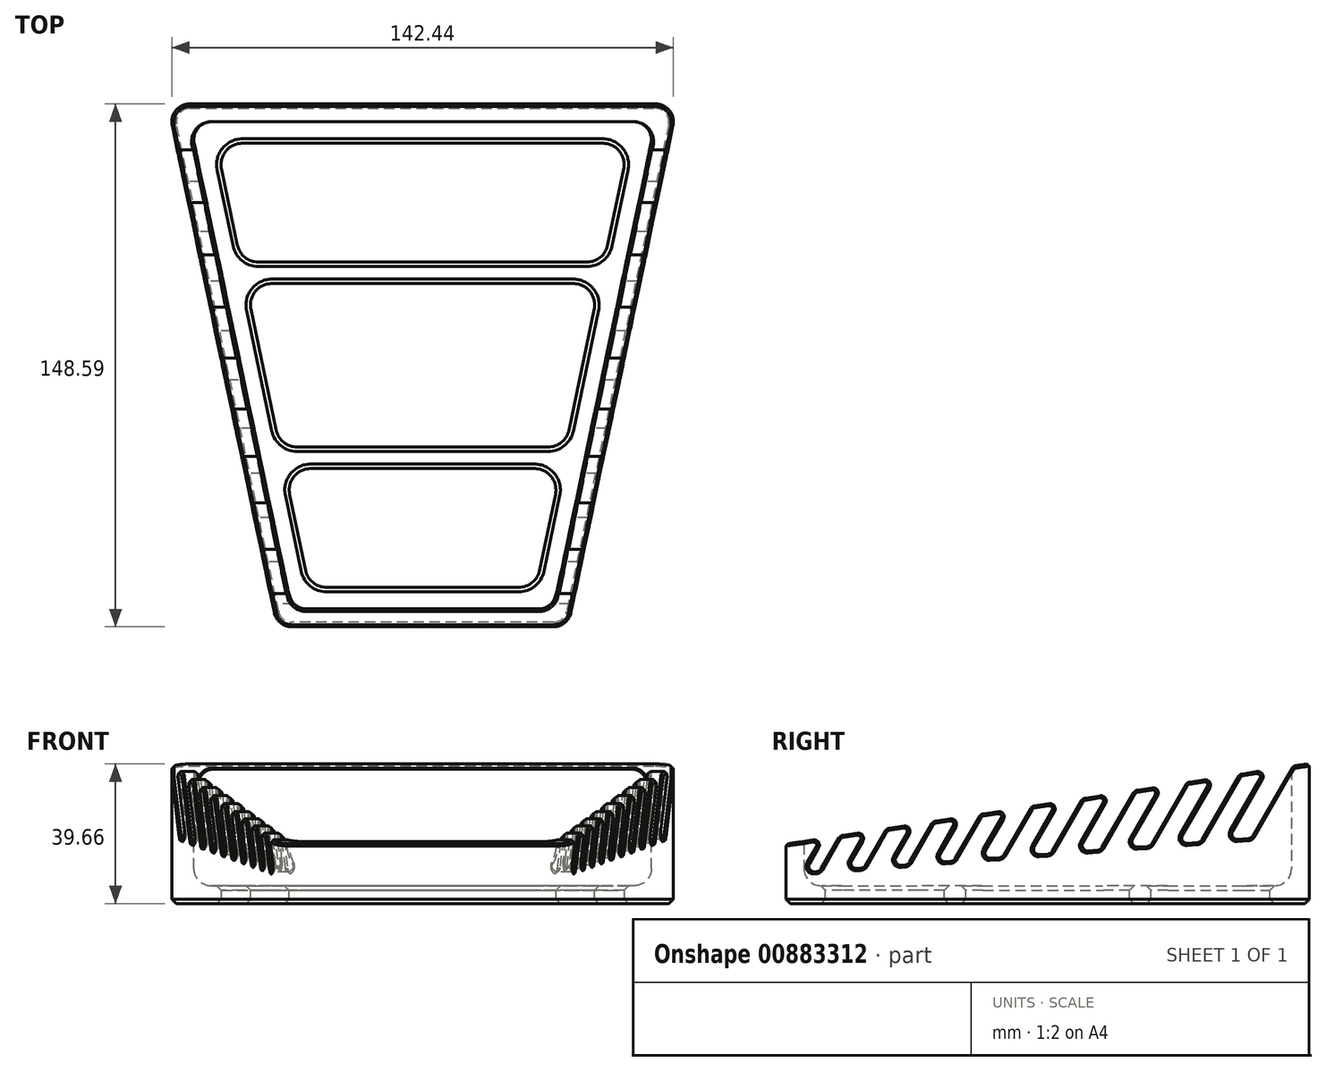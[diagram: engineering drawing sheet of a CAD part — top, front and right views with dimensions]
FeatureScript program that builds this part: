
annotation { "Feature Type Name" : "Feature", "Feature Type Description" : "" }
export const myFeature = defineFeature(function(context is Context, id is Id, definition is map)
    precondition{}
    {
        {
            var Q0;
            Q0=qCreatedBy(makeId("Top.planeOp"),FACE);
            var sketch = newSketch(context, id + "F0", { "sketchPlane" : qUnion([Q0])});
            skLineSegment(sketch, "E0", {"start": v(0, 200.12) * mm, "end": v(0, 0) * mm, "construction": true});
            skLineSegment(sketch, "E1", {"start": v(0, 0) * mm, "end": v(243.38, 0) * mm, "construction": true});
            skLineSegment(sketch, "E2", {"start": v(-72.4, 148.6) * mm, "end": v(72.4, 148.6) * mm});
            skLineSegment(sketch, "E3", {"start": v(72.4, 148.6) * mm, "end": v(41.28, 0) * mm});
            skLineSegment(sketch, "E4", {"start": v(41.28, 0) * mm, "end": v(-41.27, 0) * mm});
            skLineSegment(sketch, "E5", {"start": v(-41.27, 0) * mm, "end": v(-72.4, 148.6) * mm});
            skSolve(sketch);
        }
        {
            var Q0;
            Q0=makeQuery(id+"F0.imprint","IMPRINT",FACE,{"disambiguationData":[TD([[makeQuery(id+"F0.imprint","IMPRINT",EDGE,{"derivedFrom":sQuery(id+"F0.wireOp",EDGE,"E2")}),-1.0]])]});
            extrude(context, id + "F1", {"entities" : qUnion([Q0]), "depth" : 50.8 * mm, "offsetDistance" : 25.4 * mm});
        }
        {
            var Q0;
            Q0=qCreatedBy(makeId("Right.planeOp"),FACE);
            var sketch = newSketch(context, id + "F2", { "sketchPlane" : qUnion([Q0])});
            skLineSegment(sketch, "E6", {"start": v(0, 88.7) * mm, "end": v(0, 0) * mm, "construction": true});
            skLineSegment(sketch, "E7", {"start": v(0, 0) * mm, "end": v(187.78, 0) * mm, "construction": true});
            skCircle(sketch, "E8", {"center": v(130.24, 18.35) * mm, "radius": 18.35 * mm, "construction": true});
            skLineSegment(sketch, "E9", {"start": v(130.24, 18.35) * mm, "end": v(9.08, 9.08) * mm, "construction": true});
            skLineSegment(sketch, "E10", {"start": v(17.54, 5.78) * mm, "end": v(114.68, 8.63) * mm, "construction": true});
            skCircle(sketch, "E11", {"center": v(9.08, 9.08) * mm, "radius": 9.08 * mm, "construction": true});
            skLineSegment(sketch, "E12", {"start": v(127.45, 36.49) * mm, "end": v(7.7, 18.06) * mm, "construction": true});
            skSolve(sketch);
        }
        {
            var Q0;
            Q0=makeQuery(id+"F1.opExtrude","CAP_FACE",FACE,{"disambiguationData":[OSD([sQuery(id+"F0.wireOp",EDGE,"E2"),sQuery(id+"F0.wireOp",EDGE,"E3"),sQuery(id+"F0.wireOp",EDGE,"E4"),sQuery(id+"F0.wireOp",EDGE,"E5")])],"isStart":false});
            shell(context, id + "F3", {"entities" : qUnion([Q0]), "thickness" : 5.08 * mm});
        }
        {
            var Q0;
            Q0=qCreatedBy(makeId("Right.planeOp"),FACE);
            var sketch = newSketch(context, id + "F4", { "sketchPlane" : qUnion([Q0])});
            skLineSegment(sketch, "E13", {"start": v(0, 69.39) * mm, "end": v(0, 0) * mm, "construction": true});
            skLineSegment(sketch, "E14", {"start": v(0, 0) * mm, "end": v(193.07, 0) * mm, "construction": true});
            skLineSegment(sketch, "E15", {"start": v(-4.75, 16.16) * mm, "end": v(121.9, 35.66) * mm, "construction": true});
            skLineSegment(sketch, "E16", {"start": v(13.1, 18.91) * mm, "end": v(7.35, 8.97) * mm, "construction": true});
            skLineSegment(sketch, "E17", {"start": v(25.97, 20.9) * mm, "end": v(19.63, 9.91) * mm, "construction": true});
            skLineSegment(sketch, "E18", {"start": v(39.17, 22.93) * mm, "end": v(32.2, 10.88) * mm, "construction": true});
            skLineSegment(sketch, "E19", {"start": v(52.53, 24.98) * mm, "end": v(44.94, 11.85) * mm, "construction": true});
            skLineSegment(sketch, "E20", {"start": v(66.53, 27.14) * mm, "end": v(58.3, 12.87) * mm, "construction": true});
            skLineSegment(sketch, "E21", {"start": v(81.01, 29.37) * mm, "end": v(72.1, 13.93) * mm, "construction": true});
            skLineSegment(sketch, "E22", {"start": v(95.66, 31.62) * mm, "end": v(86.06, 15) * mm, "construction": true});
            skLineSegment(sketch, "E23", {"start": v(110.47, 33.9) * mm, "end": v(100.18, 16.08) * mm, "construction": true});
            skLineSegment(sketch, "E24", {"start": v(113.85, 34.42) * mm, "end": v(121.9, 35.66) * mm});
            skLineSegment(sketch, "E25", {"start": v(161.29, 41.72) * mm, "end": v(161.29, 63.5) * mm});
            skLineSegment(sketch, "E26", {"start": v(161.29, 63.5) * mm, "end": v(-12.7, 63.5) * mm});
            skLineSegment(sketch, "E27", {"start": v(-12.7, 63.5) * mm, "end": v(-12.7, 14.94) * mm});
            skLineSegment(sketch, "E28", {"start": v(-12.7, 14.94) * mm, "end": v(10.84, 18.56) * mm});
            skLineSegment(sketch, "E29", {"start": v(113.85, 34.42) * mm, "end": v(103.4, 16.32) * mm});
            skLineSegment(sketch, "E30", {"start": v(96.96, 15.83) * mm, "end": v(107.09, 33.38) * mm});
            skLineSegment(sketch, "E31", {"start": v(107.09, 33.38) * mm, "end": v(99.04, 32.14) * mm});
            skLineSegment(sketch, "E32", {"start": v(99.04, 32.14) * mm, "end": v(89.28, 15.24) * mm});
            skLineSegment(sketch, "E33", {"start": v(82.84, 14.75) * mm, "end": v(92.28, 31.1) * mm});
            skLineSegment(sketch, "E34", {"start": v(92.28, 31.1) * mm, "end": v(84.23, 29.86) * mm});
            skLineSegment(sketch, "E35", {"start": v(84.23, 29.86) * mm, "end": v(75.17, 14.16) * mm});
            skLineSegment(sketch, "E36", {"start": v(69.03, 13.7) * mm, "end": v(77.8, 28.87) * mm});
            skLineSegment(sketch, "E37", {"start": v(77.8, 28.87) * mm, "end": v(69.75, 27.63) * mm});
            skLineSegment(sketch, "E38", {"start": v(69.75, 27.63) * mm, "end": v(61.36, 13.1) * mm});
            skLineSegment(sketch, "E39", {"start": v(55.22, 12.64) * mm, "end": v(63.3, 26.64) * mm});
            skLineSegment(sketch, "E40", {"start": v(63.3, 26.64) * mm, "end": v(55.26, 25.4) * mm});
            skLineSegment(sketch, "E41", {"start": v(55.26, 25.4) * mm, "end": v(47.55, 12.05) * mm});
            skLineSegment(sketch, "E42", {"start": v(42.34, 11.65) * mm, "end": v(49.79, 24.56) * mm});
            skLineSegment(sketch, "E43", {"start": v(49.79, 24.56) * mm, "end": v(41.74, 23.32) * mm});
            skLineSegment(sketch, "E44", {"start": v(41.74, 23.32) * mm, "end": v(34.66, 11.06) * mm});
            skLineSegment(sketch, "E45", {"start": v(29.76, 10.69) * mm, "end": v(36.6, 22.53) * mm});
            skLineSegment(sketch, "E46", {"start": v(36.6, 22.53) * mm, "end": v(28.54, 21.29) * mm});
            skLineSegment(sketch, "E47", {"start": v(28.54, 21.29) * mm, "end": v(22.08, 10.1) * mm});
            skLineSegment(sketch, "E48", {"start": v(17.17, 9.73) * mm, "end": v(23.4, 20.5) * mm});
            skLineSegment(sketch, "E49", {"start": v(23.4, 20.5) * mm, "end": v(15.35, 19.26) * mm});
            skLineSegment(sketch, "E50", {"start": v(15.35, 19.26) * mm, "end": v(9.5, 9.14) * mm});
            skLineSegment(sketch, "E51", {"start": v(5.2, 8.8) * mm, "end": v(10.84, 18.56) * mm});
            skLineSegment(sketch, "E52", {"start": v(5.2, 8.8) * mm, "end": v(146.22, 19.6) * mm, "construction": true});
            skPoint(sketch, "E53.orphan", {"position": v(97.29, 11.07) * mm});
            skLineSegment(sketch, "E54", {"start": v(103.4, 16.32) * mm, "end": v(96.96, 15.83) * mm});
            skLineSegment(sketch, "E55", {"start": v(89.28, 15.24) * mm, "end": v(82.84, 14.75) * mm});
            skLineSegment(sketch, "E56", {"start": v(69.03, 13.7) * mm, "end": v(75.17, 14.16) * mm});
            skLineSegment(sketch, "E57", {"start": v(61.36, 13.1) * mm, "end": v(55.22, 12.64) * mm});
            skLineSegment(sketch, "E58", {"start": v(47.55, 12.05) * mm, "end": v(42.34, 11.65) * mm});
            skLineSegment(sketch, "E59", {"start": v(34.66, 11.06) * mm, "end": v(29.76, 10.69) * mm});
            skLineSegment(sketch, "E60", {"start": v(22.08, 10.1) * mm, "end": v(17.17, 9.73) * mm});
            skLineSegment(sketch, "E61", {"start": v(9.5, 9.14) * mm, "end": v(5.2, 8.8) * mm});
            skLineSegment(sketch, "E62", {"start": v(125.36, 36.2) * mm, "end": v(114.37, 17.16) * mm, "construction": true});
            skLineSegment(sketch, "E63", {"start": v(140.4, 38.5) * mm, "end": v(128.71, 18.26) * mm, "construction": true});
            skLineSegment(sketch, "E64", {"start": v(121.9, 35.66) * mm, "end": v(111.07, 16.91) * mm});
            skLineSegment(sketch, "E65", {"start": v(111.07, 16.91) * mm, "end": v(117.67, 17.42) * mm});
            skLineSegment(sketch, "E66", {"start": v(117.67, 17.42) * mm, "end": v(128.82, 36.73) * mm});
            skLineSegment(sketch, "E67.trimOffspring", {"start": v(128.82, 36.73) * mm, "end": v(136.86, 37.96) * mm, "construction": true});
            skLineSegment(sketch, "E68.trimOffspring", {"start": v(128.82, 36.73) * mm, "end": v(136.86, 37.96) * mm});
            skLineSegment(sketch, "E69", {"start": v(136.86, 37.96) * mm, "end": v(125.34, 18) * mm});
            skLineSegment(sketch, "E70", {"start": v(125.34, 18) * mm, "end": v(132.09, 18.52) * mm});
            skLineSegment(sketch, "E71", {"start": v(132.09, 18.52) * mm, "end": v(143.95, 39.06) * mm});
            skLineSegment(sketch, "E72.trimOffspring", {"start": v(161.29, 41.72) * mm, "end": v(193.55, 46.7) * mm, "construction": true});
            skLineSegment(sketch, "E73.trimOffspring", {"start": v(143.95, 39.06) * mm, "end": v(161.29, 41.72) * mm});
            skSolve(sketch);
        }
        {
            var Q0;
            Q0=qSketchRegion(id+"F4",true);
            extrude(context, id + "F5", {"entities" : qUnion([Q0]), "operationType" : NewBodyOperationType.REMOVE, "endBound" : BoundingType.THROUGH_ALL, "oppositeDirection" : true, "depth" : 25.4 * mm, "offsetDistance" : 25.4 * mm, "hasSecondDirection" : true, "secondDirectionBound" : SecondDirectionBoundingType.THROUGH_ALL, "secondDirectionOppositeDirection" : false, "secondDirectionDepth" : 25.4 * mm});
        }
        {
            var Q0;
            Q0=makeQuery(id+"F3.opShell","OFFSET_FACE",FACE,{"disambiguationData":[OSD([sQuery(id+"F0.wireOp",EDGE,"E2"),sQuery(id+"F0.wireOp",EDGE,"E3"),sQuery(id+"F0.wireOp",EDGE,"E4"),sQuery(id+"F0.wireOp",EDGE,"E5")])]});
            var sketch = newSketch(context, id + "F6", { "sketchPlane" : qUnion([Q0])});
            skLineSegment(sketch, "E74", {"start": v(-151.17, 0) * mm, "end": v(0, 0) * mm, "construction": true});
            skLineSegment(sketch, "E75", {"start": v(0, 0) * mm, "end": v(0, 307.09) * mm, "construction": true});
            skLineSegment(sketch, "E76", {"start": v(-32.2, 11.18) * mm, "end": v(32.2, 11.18) * mm});
            skLineSegment(sketch, "E77", {"start": v(32.2, 11.18) * mm, "end": v(39.27, 44.96) * mm});
            skLineSegment(sketch, "E78", {"start": v(58.63, 137.41) * mm, "end": v(-58.63, 137.41) * mm});
            skLineSegment(sketch, "E79", {"start": v(-58.63, 137.41) * mm, "end": v(-51.56, 103.63) * mm});
            skLineSegment(sketch, "E80", {"start": v(-39.9, 48) * mm, "end": v(39.9, 48) * mm, "construction": true});
            skLineSegment(sketch, "E81", {"start": v(-50.92, 100.58) * mm, "end": v(50.92, 100.58) * mm, "construction": true});
            skLineSegment(sketch, "E82", {"start": v(-39.27, 44.96) * mm, "end": v(39.27, 44.96) * mm});
            skLineSegment(sketch, "E83", {"start": v(-40.55, 51.05) * mm, "end": v(40.55, 51.05) * mm});
            skLineSegment(sketch, "E84", {"start": v(-50.28, 97.54) * mm, "end": v(50.28, 97.54) * mm});
            skLineSegment(sketch, "E85", {"start": v(-51.56, 103.63) * mm, "end": v(51.56, 103.63) * mm});
            skLineSegment(sketch, "E86.trimOffspring", {"start": v(-39.27, 44.96) * mm, "end": v(-32.2, 11.18) * mm});
            skLineSegment(sketch, "E87.trimOffspring", {"start": v(40.55, 51.05) * mm, "end": v(50.28, 97.54) * mm});
            skLineSegment(sketch, "E88.trimOffspring", {"start": v(51.56, 103.63) * mm, "end": v(58.63, 137.41) * mm});
            skLineSegment(sketch, "E89.trimOffspring", {"start": v(-50.28, 97.54) * mm, "end": v(-40.55, 51.05) * mm});
            skSolve(sketch);
        }
        {
            var Q0;
            Q0=makeQuery(id+"F6.imprint","IMPRINT",FACE,{"disambiguationData":[TD([[makeQuery(id+"F6.imprint","IMPRINT",EDGE,{"derivedFrom":sQuery(id+"F6.wireOp",EDGE,"E78")}),1.0]])]});
            var Q1;
            Q1=makeQuery(id+"F6.imprint","IMPRINT",FACE,{"disambiguationData":[TD([[makeQuery(id+"F6.imprint","IMPRINT",EDGE,{"derivedFrom":sQuery(id+"F6.wireOp",EDGE,"E83")}),1.0]])]});
            var Q2;
            Q2=makeQuery(id+"F6.imprint","IMPRINT",FACE,{"disambiguationData":[TD([[makeQuery(id+"F6.imprint","IMPRINT",EDGE,{"derivedFrom":sQuery(id+"F6.wireOp",EDGE,"E76")}),1.0]])]});
            extrude(context, id + "F7", {"entities" : qUnion([Q0, Q1, Q2]), "operationType" : NewBodyOperationType.REMOVE, "endBound" : BoundingType.THROUGH_ALL, "oppositeDirection" : true, "depth" : 25.4 * mm, "offsetDistance" : 25.4 * mm});
        }
        {
            var Q0;
            Q0=makeQuery(id+"F7.boolean.opBoolean","COPY",EDGE,{"derivedFrom":makeQuery(id+"F7.opExtrude","SWEPT_EDGE",EDGE,{"disambiguationData":[OSD([sQuery(id+"F6.wireOp",EDGE,"E78"),sQuery(id+"F6.wireOp",EDGE,"E79")])]})});
            var Q1;
            Q1=makeQuery(id+"F7.boolean.opBoolean","COPY",EDGE,{"derivedFrom":makeQuery(id+"F7.opExtrude","SWEPT_EDGE",EDGE,{"disambiguationData":[OSD([sQuery(id+"F6.wireOp",EDGE,"E78"),sQuery(id+"F6.wireOp",EDGE,"E88.trimOffspring")])]})});
            var Q2;
            Q2=makeQuery(id+"F7.boolean.opBoolean","COPY",EDGE,{"derivedFrom":makeQuery(id+"F7.opExtrude","SWEPT_EDGE",EDGE,{"disambiguationData":[OSD([sQuery(id+"F6.wireOp",EDGE,"E84"),sQuery(id+"F6.wireOp",EDGE,"E87.trimOffspring")])]})});
            var Q3;
            Q3=makeQuery(id+"F7.boolean.opBoolean","COPY",EDGE,{"derivedFrom":makeQuery(id+"F7.opExtrude","SWEPT_EDGE",EDGE,{"disambiguationData":[OSD([sQuery(id+"F6.wireOp",EDGE,"E77"),sQuery(id+"F6.wireOp",EDGE,"E82")])]})});
            var Q4;
            Q4=makeQuery(id+"F7.boolean.opBoolean","COPY",EDGE,{"derivedFrom":makeQuery(id+"F7.opExtrude","SWEPT_EDGE",EDGE,{"disambiguationData":[OSD([sQuery(id+"F6.wireOp",EDGE,"E76"),sQuery(id+"F6.wireOp",EDGE,"E77")])]})});
            var Q5;
            Q5=makeQuery(id+"F7.boolean.opBoolean","COPY",EDGE,{"derivedFrom":makeQuery(id+"F7.opExtrude","SWEPT_EDGE",EDGE,{"disambiguationData":[OSD([sQuery(id+"F6.wireOp",EDGE,"E83"),sQuery(id+"F6.wireOp",EDGE,"E87.trimOffspring")])]})});
            var Q6;
            Q6=makeQuery(id+"F7.boolean.opBoolean","COPY",EDGE,{"derivedFrom":makeQuery(id+"F7.opExtrude","SWEPT_EDGE",EDGE,{"disambiguationData":[OSD([sQuery(id+"F6.wireOp",EDGE,"E85"),sQuery(id+"F6.wireOp",EDGE,"E88.trimOffspring")])]})});
            var Q7;
            Q7=makeQuery(id+"F7.boolean.opBoolean","COPY",EDGE,{"derivedFrom":makeQuery(id+"F7.opExtrude","SWEPT_EDGE",EDGE,{"disambiguationData":[OSD([sQuery(id+"F6.wireOp",EDGE,"E76"),sQuery(id+"F6.wireOp",EDGE,"E86.trimOffspring")])]})});
            var Q8;
            Q8=makeQuery(id+"F7.boolean.opBoolean","COPY",EDGE,{"derivedFrom":makeQuery(id+"F7.opExtrude","SWEPT_EDGE",EDGE,{"disambiguationData":[OSD([sQuery(id+"F6.wireOp",EDGE,"E83"),sQuery(id+"F6.wireOp",EDGE,"E89.trimOffspring")])]})});
            var Q9;
            Q9=makeQuery(id+"F7.boolean.opBoolean","COPY",EDGE,{"derivedFrom":makeQuery(id+"F7.opExtrude","SWEPT_EDGE",EDGE,{"disambiguationData":[OSD([sQuery(id+"F6.wireOp",EDGE,"E79"),sQuery(id+"F6.wireOp",EDGE,"E85")])]})});
            var Q10;
            Q10=makeQuery(id+"F7.boolean.opBoolean","COPY",EDGE,{"derivedFrom":makeQuery(id+"F7.opExtrude","SWEPT_EDGE",EDGE,{"disambiguationData":[OSD([sQuery(id+"F6.wireOp",EDGE,"E84"),sQuery(id+"F6.wireOp",EDGE,"E89.trimOffspring")])]})});
            var Q11;
            Q11=makeQuery(id+"F7.boolean.opBoolean","COPY",EDGE,{"derivedFrom":makeQuery(id+"F7.opExtrude","SWEPT_EDGE",EDGE,{"disambiguationData":[OSD([sQuery(id+"F6.wireOp",EDGE,"E82"),sQuery(id+"F6.wireOp",EDGE,"E86.trimOffspring")])]})});
            fillet(context, id + "F8", {"entities" : qUnion([Q0, Q1, Q2, Q3, Q4, Q5, Q6, Q7, Q8, Q9, Q10, Q11]), "radius" : 6.1 * mm, "tangentPropagation" : true, "allowEdgeOverflow" : false});
        }
        {
            var Q0;
            Q0=makeQuery(id+"F3.opShell","OFFSET_EDGE",EDGE,{"disambiguationData":[OSD([sQuery(id+"F0.wireOp",EDGE,"E2"),sQuery(id+"F0.wireOp",EDGE,"E3")])]});
            var Q1;
            Q1=makeQuery(id+"F3.opShell","OFFSET_EDGE",EDGE,{"disambiguationData":[OSD([sQuery(id+"F0.wireOp",EDGE,"E2"),sQuery(id+"F0.wireOp",EDGE,"E5")])]});
            var Q2;
            Q2=makeQuery(id+"F3.opShell","OFFSET_EDGE",EDGE,{"disambiguationData":[OSD([sQuery(id+"F0.wireOp",EDGE,"E4"),sQuery(id+"F0.wireOp",EDGE,"E5")])]});
            var Q3;
            Q3=makeQuery(id+"F3.opShell","OFFSET_EDGE",EDGE,{"disambiguationData":[OSD([sQuery(id+"F0.wireOp",EDGE,"E3"),sQuery(id+"F0.wireOp",EDGE,"E4")])]});
            var Q4;
            Q4=makeQuery(id+"F1.opExtrude","SWEPT_EDGE",EDGE,{"disambiguationData":[OSD([sQuery(id+"F0.wireOp",EDGE,"E2"),sQuery(id+"F0.wireOp",EDGE,"E5")])]});
            var Q5;
            Q5=makeQuery(id+"F1.opExtrude","SWEPT_EDGE",EDGE,{"disambiguationData":[OSD([sQuery(id+"F0.wireOp",EDGE,"E4"),sQuery(id+"F0.wireOp",EDGE,"E5")])]});
            var Q6;
            Q6=makeQuery(id+"F1.opExtrude","SWEPT_EDGE",EDGE,{"disambiguationData":[OSD([sQuery(id+"F0.wireOp",EDGE,"E3"),sQuery(id+"F0.wireOp",EDGE,"E4")])]});
            var Q7;
            Q7=makeQuery(id+"F1.opExtrude","SWEPT_EDGE",EDGE,{"disambiguationData":[OSD([sQuery(id+"F0.wireOp",EDGE,"E2"),sQuery(id+"F0.wireOp",EDGE,"E3")])]});
            fillet(context, id + "F9", {"entities" : qUnion([Q0, Q1, Q2, Q3, Q4, Q5, Q6, Q7]), "radius" : 5.08 * mm, "tangentPropagation" : true, "allowEdgeOverflow" : false});
        }
        {
            var Q0;
            {var subQ0=sQuery(id+"F0.wireOp",EDGE,"E5");var subQ1=sQuery(id+"F0.wireOp",EDGE,"E2");Q0=makeQuery(id+"F9.opFillet","BLEND_EDGE",EDGE,{"blendedFrom":[makeQuery(id+"F3.opShell","OFFSET_EDGE",EDGE,{"disambiguationData":[OSD([subQ1,subQ0])]}),makeQuery(id+"F3.opShell","OFFSET_FACE",FACE,{"disambiguationData":[OSD([subQ1,sQuery(id+"F0.wireOp",EDGE,"E3"),sQuery(id+"F0.wireOp",EDGE,"E4"),subQ0])]})],"blendedInto":[makeQuery(id+"F3.opShell","OFFSET_FACE",FACE,{"disambiguationData":[OSD([subQ1,sQuery(id+"F0.wireOp",EDGE,"E3"),sQuery(id+"F0.wireOp",EDGE,"E4"),subQ0])]})]});}
            var Q1;
            {var subQ0=sQuery(id+"F0.wireOp",EDGE,"E5");Q1=makeQuery(id+"F3.opShell","OFFSET_EDGE",EDGE,{"disambiguationData":[OSD([subQ0]),TDD([makeQuery(id+"F1.opExtrude","CAP_EDGE",EDGE,{"disambiguationData":[OSD([subQ0])],"isStart":true})])]});}
            var Q2;
            {var subQ0=sQuery(id+"F0.wireOp",EDGE,"E2");Q2=makeQuery(id+"F3.opShell","OFFSET_EDGE",EDGE,{"disambiguationData":[OSD([subQ0]),TDD([makeQuery(id+"F1.opExtrude","CAP_EDGE",EDGE,{"disambiguationData":[OSD([subQ0])],"isStart":true})])]});}
            var Q3;
            {var subQ0=sQuery(id+"F0.wireOp",EDGE,"E3");var subQ1=sQuery(id+"F0.wireOp",EDGE,"E2");Q3=makeQuery(id+"F9.opFillet","BLEND_EDGE",EDGE,{"blendedFrom":[makeQuery(id+"F3.opShell","OFFSET_EDGE",EDGE,{"disambiguationData":[OSD([subQ1,subQ0])]}),makeQuery(id+"F3.opShell","OFFSET_FACE",FACE,{"disambiguationData":[OSD([subQ1,subQ0,sQuery(id+"F0.wireOp",EDGE,"E4"),sQuery(id+"F0.wireOp",EDGE,"E5")])]})],"blendedInto":[makeQuery(id+"F3.opShell","OFFSET_FACE",FACE,{"disambiguationData":[OSD([subQ1,subQ0,sQuery(id+"F0.wireOp",EDGE,"E4"),sQuery(id+"F0.wireOp",EDGE,"E5")])]})]});}
            var Q4;
            {var subQ0=sQuery(id+"F0.wireOp",EDGE,"E3");Q4=makeQuery(id+"F3.opShell","OFFSET_EDGE",EDGE,{"disambiguationData":[OSD([subQ0]),TDD([makeQuery(id+"F1.opExtrude","CAP_EDGE",EDGE,{"disambiguationData":[OSD([subQ0])],"isStart":true})])]});}
            var Q5;
            {var subQ0=sQuery(id+"F0.wireOp",EDGE,"E4");var subQ1=sQuery(id+"F0.wireOp",EDGE,"E3");Q5=makeQuery(id+"F9.opFillet","BLEND_EDGE",EDGE,{"blendedFrom":[makeQuery(id+"F3.opShell","OFFSET_EDGE",EDGE,{"disambiguationData":[OSD([subQ1,subQ0])]}),makeQuery(id+"F3.opShell","OFFSET_FACE",FACE,{"disambiguationData":[OSD([sQuery(id+"F0.wireOp",EDGE,"E2"),subQ1,subQ0,sQuery(id+"F0.wireOp",EDGE,"E5")])]})],"blendedInto":[makeQuery(id+"F3.opShell","OFFSET_FACE",FACE,{"disambiguationData":[OSD([sQuery(id+"F0.wireOp",EDGE,"E2"),subQ1,subQ0,sQuery(id+"F0.wireOp",EDGE,"E5")])]})]});}
            var Q6;
            {var subQ0=sQuery(id+"F0.wireOp",EDGE,"E4");Q6=makeQuery(id+"F3.opShell","OFFSET_EDGE",EDGE,{"disambiguationData":[OSD([subQ0]),TDD([makeQuery(id+"F1.opExtrude","CAP_EDGE",EDGE,{"disambiguationData":[OSD([subQ0])],"isStart":true})])]});}
            fillet(context, id + "F10", {"entities" : qUnion([Q0, Q1, Q2, Q3, Q4, Q5, Q6]), "radius" : 4.83 * mm, "tangentPropagation" : true, "allowEdgeOverflow" : false});
        }
        {
            var Q0;
            {var subQ0=sQuery(id+"F0.wireOp",EDGE,"E3");var subQ1=sQuery(id+"F4.wireOp",EDGE,"E50");var subQ2=sQuery(id+"F4.wireOp",EDGE,"SIKbP8tO-JJDS-i6Zd-XH3O-vxsOhT12Df2S");Q0=makeQuery(id+"F5.boolean.opBoolean","COPY",EDGE,{"disambiguationData":[TD([makeQuery(id+"F1.opExtrude","SWEPT_FACE",FACE,{"disambiguationData":[OSD([subQ0])]})])],"derivedFrom":makeQuery(id+"F5.opExtrude","SWEPT_EDGE",EDGE,{"disambiguationData":[OSD([subQ1,subQ2])]})});}
            var Q1;
            {var subQ0=sQuery(id+"F0.wireOp",EDGE,"E3");var subQ1=sQuery(id+"F4.wireOp",EDGE,"SIKbP8tO-JJDS-i6Zd-XH3O-vxsOhT12Df2S");var subQ2=sQuery(id+"F4.wireOp",EDGE,"E51");Q1=makeQuery(id+"F5.boolean.opBoolean","COPY",EDGE,{"disambiguationData":[TD([makeQuery(id+"F1.opExtrude","SWEPT_FACE",FACE,{"disambiguationData":[OSD([subQ0])]})])],"derivedFrom":makeQuery(id+"F5.opExtrude","SWEPT_EDGE",EDGE,{"disambiguationData":[OSD([subQ1,subQ2])]})});}
            var Q2;
            {var subQ0=sQuery(id+"F0.wireOp",EDGE,"E3");var subQ1=sQuery(id+"F4.wireOp",EDGE,"E48");var subQ2=sQuery(id+"F4.wireOp",EDGE,"sNC93h9R-KJSe-uxuB-Bmqh-0vs0cjGmztf7");Q2=makeQuery(id+"F5.boolean.opBoolean","COPY",EDGE,{"disambiguationData":[TD([makeQuery(id+"F1.opExtrude","SWEPT_FACE",FACE,{"disambiguationData":[OSD([subQ0])]})])],"derivedFrom":makeQuery(id+"F5.opExtrude","SWEPT_EDGE",EDGE,{"disambiguationData":[OSD([subQ2,subQ1])]})});}
            var Q3;
            {var subQ0=sQuery(id+"F0.wireOp",EDGE,"E3");var subQ1=sQuery(id+"F4.wireOp",EDGE,"E47");var subQ2=sQuery(id+"F4.wireOp",EDGE,"sNC93h9R-KJSe-uxuB-Bmqh-0vs0cjGmztf7");Q3=makeQuery(id+"F5.boolean.opBoolean","COPY",EDGE,{"disambiguationData":[TD([makeQuery(id+"F1.opExtrude","SWEPT_FACE",FACE,{"disambiguationData":[OSD([subQ0])]})])],"derivedFrom":makeQuery(id+"F5.opExtrude","SWEPT_EDGE",EDGE,{"disambiguationData":[OSD([subQ1,subQ2])]})});}
            var Q4;
            {var subQ0=sQuery(id+"F0.wireOp",EDGE,"E3");var subQ1=sQuery(id+"F4.wireOp",EDGE,"BCbbEfCC-h4Tc-u2UY-SoFu-l8d2SlAXyGNP");var subQ2=sQuery(id+"F4.wireOp",EDGE,"E44");Q4=makeQuery(id+"F5.boolean.opBoolean","COPY",EDGE,{"disambiguationData":[TD([makeQuery(id+"F1.opExtrude","SWEPT_FACE",FACE,{"disambiguationData":[OSD([subQ0])]})])],"derivedFrom":makeQuery(id+"F5.opExtrude","SWEPT_EDGE",EDGE,{"disambiguationData":[OSD([subQ2,subQ1])]})});}
            var Q5;
            {var subQ0=sQuery(id+"F0.wireOp",EDGE,"E3");var subQ1=sQuery(id+"F4.wireOp",EDGE,"E41");var subQ2=sQuery(id+"F4.wireOp",EDGE,"ZfMw33CZ-0StR-yFHK-VDgl-Y98y6gqkxQnj");Q5=makeQuery(id+"F5.boolean.opBoolean","COPY",EDGE,{"disambiguationData":[TD([makeQuery(id+"F1.opExtrude","SWEPT_FACE",FACE,{"disambiguationData":[OSD([subQ0])]})])],"derivedFrom":makeQuery(id+"F5.opExtrude","SWEPT_EDGE",EDGE,{"disambiguationData":[OSD([subQ1,subQ2])]})});}
            var Q6;
            {var subQ0=sQuery(id+"F0.wireOp",EDGE,"E3");var subQ1=sQuery(id+"F4.wireOp",EDGE,"E38");var subQ2=sQuery(id+"F4.wireOp",EDGE,"ipyGLaIt-meO7-XkRn-SYox-uSJgsCgIzxGM");Q6=makeQuery(id+"F5.boolean.opBoolean","COPY",EDGE,{"disambiguationData":[TD([makeQuery(id+"F1.opExtrude","SWEPT_FACE",FACE,{"disambiguationData":[OSD([subQ0])]})])],"derivedFrom":makeQuery(id+"F5.opExtrude","SWEPT_EDGE",EDGE,{"disambiguationData":[OSD([subQ1,subQ2])]})});}
            var Q7;
            {var subQ0=sQuery(id+"F0.wireOp",EDGE,"E3");var subQ1=sQuery(id+"F4.wireOp",EDGE,"E35");var subQ2=sQuery(id+"F4.wireOp",EDGE,"7qeNIu7M-td8I-Ih3K-TXT1-bYg1YDSNIcf6");Q7=makeQuery(id+"F5.boolean.opBoolean","COPY",EDGE,{"disambiguationData":[TD([makeQuery(id+"F1.opExtrude","SWEPT_FACE",FACE,{"disambiguationData":[OSD([subQ0])]})])],"derivedFrom":makeQuery(id+"F5.opExtrude","SWEPT_EDGE",EDGE,{"disambiguationData":[OSD([subQ1,subQ2])]})});}
            var Q8;
            {var subQ0=sQuery(id+"F0.wireOp",EDGE,"E3");var subQ1=sQuery(id+"F4.wireOp",EDGE,"E32");var subQ2=sQuery(id+"F4.wireOp",EDGE,"gRpP0bbj-nH9h-IPZG-9A25-aJMpr01YVRqs");Q8=makeQuery(id+"F5.boolean.opBoolean","COPY",EDGE,{"disambiguationData":[TD([makeQuery(id+"F1.opExtrude","SWEPT_FACE",FACE,{"disambiguationData":[OSD([subQ0])]})])],"derivedFrom":makeQuery(id+"F5.opExtrude","SWEPT_EDGE",EDGE,{"disambiguationData":[OSD([subQ1,subQ2])]})});}
            var Q9;
            {var subQ0=sQuery(id+"F0.wireOp",EDGE,"E3");var subQ1=sQuery(id+"F4.wireOp",EDGE,"P4BXycm8-icTH-da2u-U7mR-u9QEaXhu1Nye");var subQ2=sQuery(id+"F4.wireOp",EDGE,"E29");Q9=makeQuery(id+"F5.boolean.opBoolean","COPY",EDGE,{"disambiguationData":[TD([makeQuery(id+"F1.opExtrude","SWEPT_FACE",FACE,{"disambiguationData":[OSD([subQ0])]})])],"derivedFrom":makeQuery(id+"F5.opExtrude","SWEPT_EDGE",EDGE,{"disambiguationData":[OSD([subQ2,subQ1])]})});}
            var Q10;
            {var subQ0=sQuery(id+"F0.wireOp",EDGE,"E3");var subQ1=sQuery(id+"F4.wireOp",EDGE,"P4BXycm8-icTH-da2u-U7mR-u9QEaXhu1Nye");var subQ2=sQuery(id+"F4.wireOp",EDGE,"E30");Q10=makeQuery(id+"F5.boolean.opBoolean","COPY",EDGE,{"disambiguationData":[TD([makeQuery(id+"F1.opExtrude","SWEPT_FACE",FACE,{"disambiguationData":[OSD([subQ0])]})])],"derivedFrom":makeQuery(id+"F5.opExtrude","SWEPT_EDGE",EDGE,{"disambiguationData":[OSD([subQ1,subQ2])]})});}
            var Q11;
            {var subQ0=sQuery(id+"F0.wireOp",EDGE,"E3");var subQ1=sQuery(id+"F4.wireOp",EDGE,"E33");var subQ2=sQuery(id+"F4.wireOp",EDGE,"gRpP0bbj-nH9h-IPZG-9A25-aJMpr01YVRqs");Q11=makeQuery(id+"F5.boolean.opBoolean","COPY",EDGE,{"disambiguationData":[TD([makeQuery(id+"F1.opExtrude","SWEPT_FACE",FACE,{"disambiguationData":[OSD([subQ0])]})])],"derivedFrom":makeQuery(id+"F5.opExtrude","SWEPT_EDGE",EDGE,{"disambiguationData":[OSD([subQ2,subQ1])]})});}
            var Q12;
            {var subQ0=sQuery(id+"F0.wireOp",EDGE,"E3");var subQ1=sQuery(id+"F4.wireOp",EDGE,"7qeNIu7M-td8I-Ih3K-TXT1-bYg1YDSNIcf6");var subQ2=sQuery(id+"F4.wireOp",EDGE,"E36");Q12=makeQuery(id+"F5.boolean.opBoolean","COPY",EDGE,{"disambiguationData":[TD([makeQuery(id+"F1.opExtrude","SWEPT_FACE",FACE,{"disambiguationData":[OSD([subQ0])]})])],"derivedFrom":makeQuery(id+"F5.opExtrude","SWEPT_EDGE",EDGE,{"disambiguationData":[OSD([subQ1,subQ2])]})});}
            var Q13;
            {var subQ0=sQuery(id+"F0.wireOp",EDGE,"E3");var subQ1=sQuery(id+"F4.wireOp",EDGE,"ipyGLaIt-meO7-XkRn-SYox-uSJgsCgIzxGM");var subQ2=sQuery(id+"F4.wireOp",EDGE,"E39");Q13=makeQuery(id+"F5.boolean.opBoolean","COPY",EDGE,{"disambiguationData":[TD([makeQuery(id+"F1.opExtrude","SWEPT_FACE",FACE,{"disambiguationData":[OSD([subQ0])]})])],"derivedFrom":makeQuery(id+"F5.opExtrude","SWEPT_EDGE",EDGE,{"disambiguationData":[OSD([subQ1,subQ2])]})});}
            var Q14;
            {var subQ0=sQuery(id+"F0.wireOp",EDGE,"E3");var subQ1=sQuery(id+"F4.wireOp",EDGE,"ZfMw33CZ-0StR-yFHK-VDgl-Y98y6gqkxQnj");var subQ2=sQuery(id+"F4.wireOp",EDGE,"E42");Q14=makeQuery(id+"F5.boolean.opBoolean","COPY",EDGE,{"disambiguationData":[TD([makeQuery(id+"F1.opExtrude","SWEPT_FACE",FACE,{"disambiguationData":[OSD([subQ0])]})])],"derivedFrom":makeQuery(id+"F5.opExtrude","SWEPT_EDGE",EDGE,{"disambiguationData":[OSD([subQ1,subQ2])]})});}
            var Q15;
            {var subQ0=sQuery(id+"F0.wireOp",EDGE,"E3");var subQ1=sQuery(id+"F4.wireOp",EDGE,"BCbbEfCC-h4Tc-u2UY-SoFu-l8d2SlAXyGNP");var subQ2=sQuery(id+"F4.wireOp",EDGE,"E45");Q15=makeQuery(id+"F5.boolean.opBoolean","COPY",EDGE,{"disambiguationData":[TD([makeQuery(id+"F1.opExtrude","SWEPT_FACE",FACE,{"disambiguationData":[OSD([subQ0])]})])],"derivedFrom":makeQuery(id+"F5.opExtrude","SWEPT_EDGE",EDGE,{"disambiguationData":[OSD([subQ1,subQ2])]})});}
            var Q16;
            {var subQ0=sQuery(id+"F0.wireOp",EDGE,"E5");var subQ1=sQuery(id+"F4.wireOp",EDGE,"SIKbP8tO-JJDS-i6Zd-XH3O-vxsOhT12Df2S");var subQ2=sQuery(id+"F4.wireOp",EDGE,"E51");Q16=makeQuery(id+"F5.boolean.opBoolean","COPY",EDGE,{"disambiguationData":[TD([makeQuery(id+"F1.opExtrude","SWEPT_FACE",FACE,{"disambiguationData":[OSD([subQ0])]})])],"derivedFrom":makeQuery(id+"F5.opExtrude","SWEPT_EDGE",EDGE,{"disambiguationData":[OSD([subQ1,subQ2])]})});}
            var Q17;
            {var subQ0=sQuery(id+"F0.wireOp",EDGE,"E5");var subQ1=sQuery(id+"F4.wireOp",EDGE,"sNC93h9R-KJSe-uxuB-Bmqh-0vs0cjGmztf7");var subQ2=sQuery(id+"F4.wireOp",EDGE,"E48");Q17=makeQuery(id+"F5.boolean.opBoolean","COPY",EDGE,{"disambiguationData":[TD([makeQuery(id+"F1.opExtrude","SWEPT_FACE",FACE,{"disambiguationData":[OSD([subQ0])]})])],"derivedFrom":makeQuery(id+"F5.opExtrude","SWEPT_EDGE",EDGE,{"disambiguationData":[OSD([subQ1,subQ2])]})});}
            var Q18;
            {var subQ0=sQuery(id+"F0.wireOp",EDGE,"E5");var subQ1=sQuery(id+"F4.wireOp",EDGE,"BCbbEfCC-h4Tc-u2UY-SoFu-l8d2SlAXyGNP");var subQ2=sQuery(id+"F4.wireOp",EDGE,"E45");Q18=makeQuery(id+"F5.boolean.opBoolean","COPY",EDGE,{"disambiguationData":[TD([makeQuery(id+"F1.opExtrude","SWEPT_FACE",FACE,{"disambiguationData":[OSD([subQ0])]})])],"derivedFrom":makeQuery(id+"F5.opExtrude","SWEPT_EDGE",EDGE,{"disambiguationData":[OSD([subQ1,subQ2])]})});}
            var Q19;
            {var subQ0=sQuery(id+"F0.wireOp",EDGE,"E5");var subQ1=sQuery(id+"F4.wireOp",EDGE,"E42");var subQ2=sQuery(id+"F4.wireOp",EDGE,"ZfMw33CZ-0StR-yFHK-VDgl-Y98y6gqkxQnj");Q19=makeQuery(id+"F5.boolean.opBoolean","COPY",EDGE,{"disambiguationData":[TD([makeQuery(id+"F1.opExtrude","SWEPT_FACE",FACE,{"disambiguationData":[OSD([subQ0])]})])],"derivedFrom":makeQuery(id+"F5.opExtrude","SWEPT_EDGE",EDGE,{"disambiguationData":[OSD([subQ2,subQ1])]})});}
            var Q20;
            {var subQ0=sQuery(id+"F0.wireOp",EDGE,"E5");var subQ1=sQuery(id+"F4.wireOp",EDGE,"E50");var subQ2=sQuery(id+"F4.wireOp",EDGE,"SIKbP8tO-JJDS-i6Zd-XH3O-vxsOhT12Df2S");Q20=makeQuery(id+"F5.boolean.opBoolean","COPY",EDGE,{"disambiguationData":[TD([makeQuery(id+"F1.opExtrude","SWEPT_FACE",FACE,{"disambiguationData":[OSD([subQ0])]})])],"derivedFrom":makeQuery(id+"F5.opExtrude","SWEPT_EDGE",EDGE,{"disambiguationData":[OSD([subQ1,subQ2])]})});}
            var Q21;
            {var subQ0=sQuery(id+"F0.wireOp",EDGE,"E5");var subQ1=sQuery(id+"F4.wireOp",EDGE,"E47");var subQ2=sQuery(id+"F4.wireOp",EDGE,"sNC93h9R-KJSe-uxuB-Bmqh-0vs0cjGmztf7");Q21=makeQuery(id+"F5.boolean.opBoolean","COPY",EDGE,{"disambiguationData":[TD([makeQuery(id+"F1.opExtrude","SWEPT_FACE",FACE,{"disambiguationData":[OSD([subQ0])]})])],"derivedFrom":makeQuery(id+"F5.opExtrude","SWEPT_EDGE",EDGE,{"disambiguationData":[OSD([subQ1,subQ2])]})});}
            var Q22;
            {var subQ0=sQuery(id+"F0.wireOp",EDGE,"E5");var subQ1=sQuery(id+"F4.wireOp",EDGE,"E44");var subQ2=sQuery(id+"F4.wireOp",EDGE,"BCbbEfCC-h4Tc-u2UY-SoFu-l8d2SlAXyGNP");Q22=makeQuery(id+"F5.boolean.opBoolean","COPY",EDGE,{"disambiguationData":[TD([makeQuery(id+"F1.opExtrude","SWEPT_FACE",FACE,{"disambiguationData":[OSD([subQ0])]})])],"derivedFrom":makeQuery(id+"F5.opExtrude","SWEPT_EDGE",EDGE,{"disambiguationData":[OSD([subQ1,subQ2])]})});}
            var Q23;
            {var subQ0=sQuery(id+"F0.wireOp",EDGE,"E5");var subQ1=sQuery(id+"F4.wireOp",EDGE,"E41");var subQ2=sQuery(id+"F4.wireOp",EDGE,"ZfMw33CZ-0StR-yFHK-VDgl-Y98y6gqkxQnj");Q23=makeQuery(id+"F5.boolean.opBoolean","COPY",EDGE,{"disambiguationData":[TD([makeQuery(id+"F1.opExtrude","SWEPT_FACE",FACE,{"disambiguationData":[OSD([subQ0])]})])],"derivedFrom":makeQuery(id+"F5.opExtrude","SWEPT_EDGE",EDGE,{"disambiguationData":[OSD([subQ1,subQ2])]})});}
            var Q24;
            {var subQ0=sQuery(id+"F0.wireOp",EDGE,"E5");var subQ1=sQuery(id+"F4.wireOp",EDGE,"ipyGLaIt-meO7-XkRn-SYox-uSJgsCgIzxGM");var subQ2=sQuery(id+"F4.wireOp",EDGE,"E38");Q24=makeQuery(id+"F5.boolean.opBoolean","COPY",EDGE,{"disambiguationData":[TD([makeQuery(id+"F1.opExtrude","SWEPT_FACE",FACE,{"disambiguationData":[OSD([subQ0])]})])],"derivedFrom":makeQuery(id+"F5.opExtrude","SWEPT_EDGE",EDGE,{"disambiguationData":[OSD([subQ2,subQ1])]})});}
            var Q25;
            {var subQ0=sQuery(id+"F0.wireOp",EDGE,"E5");var subQ1=sQuery(id+"F4.wireOp",EDGE,"ipyGLaIt-meO7-XkRn-SYox-uSJgsCgIzxGM");var subQ2=sQuery(id+"F4.wireOp",EDGE,"E39");Q25=makeQuery(id+"F5.boolean.opBoolean","COPY",EDGE,{"disambiguationData":[TD([makeQuery(id+"F1.opExtrude","SWEPT_FACE",FACE,{"disambiguationData":[OSD([subQ0])]})])],"derivedFrom":makeQuery(id+"F5.opExtrude","SWEPT_EDGE",EDGE,{"disambiguationData":[OSD([subQ1,subQ2])]})});}
            var Q26;
            {var subQ0=sQuery(id+"F0.wireOp",EDGE,"E5");var subQ1=sQuery(id+"F4.wireOp",EDGE,"7qeNIu7M-td8I-Ih3K-TXT1-bYg1YDSNIcf6");var subQ2=sQuery(id+"F4.wireOp",EDGE,"E36");Q26=makeQuery(id+"F5.boolean.opBoolean","COPY",EDGE,{"disambiguationData":[TD([makeQuery(id+"F1.opExtrude","SWEPT_FACE",FACE,{"disambiguationData":[OSD([subQ0])]})])],"derivedFrom":makeQuery(id+"F5.opExtrude","SWEPT_EDGE",EDGE,{"disambiguationData":[OSD([subQ1,subQ2])]})});}
            var Q27;
            {var subQ0=sQuery(id+"F0.wireOp",EDGE,"E5");var subQ1=sQuery(id+"F4.wireOp",EDGE,"E35");var subQ2=sQuery(id+"F4.wireOp",EDGE,"7qeNIu7M-td8I-Ih3K-TXT1-bYg1YDSNIcf6");Q27=makeQuery(id+"F5.boolean.opBoolean","COPY",EDGE,{"disambiguationData":[TD([makeQuery(id+"F1.opExtrude","SWEPT_FACE",FACE,{"disambiguationData":[OSD([subQ0])]})])],"derivedFrom":makeQuery(id+"F5.opExtrude","SWEPT_EDGE",EDGE,{"disambiguationData":[OSD([subQ1,subQ2])]})});}
            var Q28;
            {var subQ0=sQuery(id+"F0.wireOp",EDGE,"E5");var subQ1=sQuery(id+"F4.wireOp",EDGE,"gRpP0bbj-nH9h-IPZG-9A25-aJMpr01YVRqs");var subQ2=sQuery(id+"F4.wireOp",EDGE,"E33");Q28=makeQuery(id+"F5.boolean.opBoolean","COPY",EDGE,{"disambiguationData":[TD([makeQuery(id+"F1.opExtrude","SWEPT_FACE",FACE,{"disambiguationData":[OSD([subQ0])]})])],"derivedFrom":makeQuery(id+"F5.opExtrude","SWEPT_EDGE",EDGE,{"disambiguationData":[OSD([subQ1,subQ2])]})});}
            var Q29;
            {var subQ0=sQuery(id+"F0.wireOp",EDGE,"E5");var subQ1=sQuery(id+"F4.wireOp",EDGE,"E32");var subQ2=sQuery(id+"F4.wireOp",EDGE,"gRpP0bbj-nH9h-IPZG-9A25-aJMpr01YVRqs");Q29=makeQuery(id+"F5.boolean.opBoolean","COPY",EDGE,{"disambiguationData":[TD([makeQuery(id+"F1.opExtrude","SWEPT_FACE",FACE,{"disambiguationData":[OSD([subQ0])]})])],"derivedFrom":makeQuery(id+"F5.opExtrude","SWEPT_EDGE",EDGE,{"disambiguationData":[OSD([subQ1,subQ2])]})});}
            var Q30;
            {var subQ0=sQuery(id+"F0.wireOp",EDGE,"E5");var subQ1=sQuery(id+"F4.wireOp",EDGE,"E29");var subQ2=sQuery(id+"F4.wireOp",EDGE,"P4BXycm8-icTH-da2u-U7mR-u9QEaXhu1Nye");Q30=makeQuery(id+"F5.boolean.opBoolean","COPY",EDGE,{"disambiguationData":[TD([makeQuery(id+"F1.opExtrude","SWEPT_FACE",FACE,{"disambiguationData":[OSD([subQ0])]})])],"derivedFrom":makeQuery(id+"F5.opExtrude","SWEPT_EDGE",EDGE,{"disambiguationData":[OSD([subQ1,subQ2])]})});}
            var Q31;
            {var subQ0=sQuery(id+"F0.wireOp",EDGE,"E5");var subQ1=sQuery(id+"F4.wireOp",EDGE,"P4BXycm8-icTH-da2u-U7mR-u9QEaXhu1Nye");var subQ2=sQuery(id+"F4.wireOp",EDGE,"E30");Q31=makeQuery(id+"F5.boolean.opBoolean","COPY",EDGE,{"disambiguationData":[TD([makeQuery(id+"F1.opExtrude","SWEPT_FACE",FACE,{"disambiguationData":[OSD([subQ0])]})])],"derivedFrom":makeQuery(id+"F5.opExtrude","SWEPT_EDGE",EDGE,{"disambiguationData":[OSD([subQ1,subQ2])]})});}
            var Q32;
            {var subQ0=sQuery(id+"F0.wireOp",EDGE,"E5");var subQ1=sQuery(id+"F4.wireOp",EDGE,"E24");var subQ2=sQuery(id+"F4.wireOp",EDGE,"E64");Q32=makeQuery(id+"F5.boolean.opBoolean","COPY",EDGE,{"disambiguationData":[TD([makeQuery(id+"F1.opExtrude","SWEPT_FACE",FACE,{"disambiguationData":[OSD([subQ0])]})])],"derivedFrom":makeQuery(id+"F5.opExtrude","SWEPT_EDGE",EDGE,{"disambiguationData":[OSD([subQ1,subQ2])]})});}
            var Q33;
            {var subQ0=sQuery(id+"F0.wireOp",EDGE,"E5");var subQ1=sQuery(id+"F4.wireOp",EDGE,"E66");var subQ2=sQuery(id+"F4.wireOp",EDGE,"E68.trimOffspring");Q33=makeQuery(id+"F5.boolean.opBoolean","COPY",EDGE,{"disambiguationData":[TD([makeQuery(id+"F1.opExtrude","SWEPT_FACE",FACE,{"disambiguationData":[OSD([subQ0])]})])],"derivedFrom":makeQuery(id+"F5.opExtrude","SWEPT_EDGE",EDGE,{"disambiguationData":[OSD([subQ1,subQ2])]})});}
            var Q34;
            {var subQ0=sQuery(id+"F0.wireOp",EDGE,"E5");var subQ1=sQuery(id+"F4.wireOp",EDGE,"E68.trimOffspring");var subQ2=sQuery(id+"F4.wireOp",EDGE,"E69");Q34=makeQuery(id+"F5.boolean.opBoolean","COPY",EDGE,{"disambiguationData":[TD([makeQuery(id+"F1.opExtrude","SWEPT_FACE",FACE,{"disambiguationData":[OSD([subQ0])]})])],"derivedFrom":makeQuery(id+"F5.opExtrude","SWEPT_EDGE",EDGE,{"disambiguationData":[OSD([subQ1,subQ2])]})});}
            var Q35;
            {var subQ0=sQuery(id+"F0.wireOp",EDGE,"E5");var subQ1=sQuery(id+"F4.wireOp",EDGE,"E73.trimOffspring");var subQ2=sQuery(id+"F4.wireOp",EDGE,"E71");Q35=makeQuery(id+"F5.boolean.opBoolean","COPY",EDGE,{"disambiguationData":[TD([makeQuery(id+"F1.opExtrude","SWEPT_FACE",FACE,{"disambiguationData":[OSD([subQ0])]})])],"derivedFrom":makeQuery(id+"F5.opExtrude","SWEPT_EDGE",EDGE,{"disambiguationData":[OSD([subQ2,subQ1])]})});}
            var Q36;
            {var subQ0=sQuery(id+"F0.wireOp",EDGE,"E5");var subQ1=sQuery(id+"F4.wireOp",EDGE,"E70");var subQ2=sQuery(id+"F4.wireOp",EDGE,"E71");Q36=makeQuery(id+"F5.boolean.opBoolean","COPY",EDGE,{"disambiguationData":[TD([makeQuery(id+"F1.opExtrude","SWEPT_FACE",FACE,{"disambiguationData":[OSD([subQ0])]})])],"derivedFrom":makeQuery(id+"F5.opExtrude","SWEPT_EDGE",EDGE,{"disambiguationData":[OSD([subQ1,subQ2])]})});}
            var Q37;
            {var subQ0=sQuery(id+"F0.wireOp",EDGE,"E5");var subQ1=sQuery(id+"F4.wireOp",EDGE,"E69");var subQ2=sQuery(id+"F4.wireOp",EDGE,"E70");Q37=makeQuery(id+"F5.boolean.opBoolean","COPY",EDGE,{"disambiguationData":[TD([makeQuery(id+"F1.opExtrude","SWEPT_FACE",FACE,{"disambiguationData":[OSD([subQ0])]})])],"derivedFrom":makeQuery(id+"F5.opExtrude","SWEPT_EDGE",EDGE,{"disambiguationData":[OSD([subQ1,subQ2])]})});}
            var Q38;
            {var subQ0=sQuery(id+"F0.wireOp",EDGE,"E5");var subQ1=sQuery(id+"F4.wireOp",EDGE,"E64");var subQ2=sQuery(id+"F4.wireOp",EDGE,"E65");Q38=makeQuery(id+"F5.boolean.opBoolean","COPY",EDGE,{"disambiguationData":[TD([makeQuery(id+"F1.opExtrude","SWEPT_FACE",FACE,{"disambiguationData":[OSD([subQ0])]})])],"derivedFrom":makeQuery(id+"F5.opExtrude","SWEPT_EDGE",EDGE,{"disambiguationData":[OSD([subQ1,subQ2])]})});}
            var Q39;
            {var subQ0=sQuery(id+"F0.wireOp",EDGE,"E5");var subQ1=sQuery(id+"F4.wireOp",EDGE,"E66");var subQ2=sQuery(id+"F4.wireOp",EDGE,"E65");Q39=makeQuery(id+"F5.boolean.opBoolean","COPY",EDGE,{"disambiguationData":[TD([makeQuery(id+"F1.opExtrude","SWEPT_FACE",FACE,{"disambiguationData":[OSD([subQ0])]})])],"derivedFrom":makeQuery(id+"F5.opExtrude","SWEPT_EDGE",EDGE,{"disambiguationData":[OSD([subQ2,subQ1])]})});}
            var Q40;
            {var subQ0=sQuery(id+"F0.wireOp",EDGE,"E3");var subQ1=sQuery(id+"F4.wireOp",EDGE,"E70");var subQ2=sQuery(id+"F4.wireOp",EDGE,"E71");Q40=makeQuery(id+"F5.boolean.opBoolean","COPY",EDGE,{"disambiguationData":[TD([makeQuery(id+"F1.opExtrude","SWEPT_FACE",FACE,{"disambiguationData":[OSD([subQ0])]})])],"derivedFrom":makeQuery(id+"F5.opExtrude","SWEPT_EDGE",EDGE,{"disambiguationData":[OSD([subQ1,subQ2])]})});}
            var Q41;
            {var subQ0=sQuery(id+"F0.wireOp",EDGE,"E3");var subQ1=sQuery(id+"F4.wireOp",EDGE,"E68.trimOffspring");var subQ2=sQuery(id+"F4.wireOp",EDGE,"E69");Q41=makeQuery(id+"F5.boolean.opBoolean","COPY",EDGE,{"disambiguationData":[TD([makeQuery(id+"F1.opExtrude","SWEPT_FACE",FACE,{"disambiguationData":[OSD([subQ0])]})])],"derivedFrom":makeQuery(id+"F5.opExtrude","SWEPT_EDGE",EDGE,{"disambiguationData":[OSD([subQ1,subQ2])]})});}
            var Q42;
            {var subQ0=sQuery(id+"F0.wireOp",EDGE,"E3");var subQ1=sQuery(id+"F4.wireOp",EDGE,"E66");var subQ2=sQuery(id+"F4.wireOp",EDGE,"E68.trimOffspring");Q42=makeQuery(id+"F5.boolean.opBoolean","COPY",EDGE,{"disambiguationData":[TD([makeQuery(id+"F1.opExtrude","SWEPT_FACE",FACE,{"disambiguationData":[OSD([subQ0])]})])],"derivedFrom":makeQuery(id+"F5.opExtrude","SWEPT_EDGE",EDGE,{"disambiguationData":[OSD([subQ1,subQ2])]})});}
            var Q43;
            {var subQ0=sQuery(id+"F0.wireOp",EDGE,"E3");var subQ1=sQuery(id+"F4.wireOp",EDGE,"E64");var subQ2=sQuery(id+"F4.wireOp",EDGE,"E24");Q43=makeQuery(id+"F5.boolean.opBoolean","COPY",EDGE,{"disambiguationData":[TD([makeQuery(id+"F1.opExtrude","SWEPT_FACE",FACE,{"disambiguationData":[OSD([subQ0])]})])],"derivedFrom":makeQuery(id+"F5.opExtrude","SWEPT_EDGE",EDGE,{"disambiguationData":[OSD([subQ2,subQ1])]})});}
            var Q44;
            {var subQ0=sQuery(id+"F0.wireOp",EDGE,"E3");var subQ1=sQuery(id+"F4.wireOp",EDGE,"E65");var subQ2=sQuery(id+"F4.wireOp",EDGE,"E66");Q44=makeQuery(id+"F5.boolean.opBoolean","COPY",EDGE,{"disambiguationData":[TD([makeQuery(id+"F1.opExtrude","SWEPT_FACE",FACE,{"disambiguationData":[OSD([subQ0])]})])],"derivedFrom":makeQuery(id+"F5.opExtrude","SWEPT_EDGE",EDGE,{"disambiguationData":[OSD([subQ1,subQ2])]})});}
            var Q45;
            {var subQ0=sQuery(id+"F0.wireOp",EDGE,"E3");var subQ1=sQuery(id+"F4.wireOp",EDGE,"E70");var subQ2=sQuery(id+"F4.wireOp",EDGE,"E69");Q45=makeQuery(id+"F5.boolean.opBoolean","COPY",EDGE,{"disambiguationData":[TD([makeQuery(id+"F1.opExtrude","SWEPT_FACE",FACE,{"disambiguationData":[OSD([subQ0])]})])],"derivedFrom":makeQuery(id+"F5.opExtrude","SWEPT_EDGE",EDGE,{"disambiguationData":[OSD([subQ2,subQ1])]})});}
            var Q46;
            {var subQ0=sQuery(id+"F0.wireOp",EDGE,"E3");var subQ1=sQuery(id+"F4.wireOp",EDGE,"E64");var subQ2=sQuery(id+"F4.wireOp",EDGE,"E65");Q46=makeQuery(id+"F5.boolean.opBoolean","COPY",EDGE,{"disambiguationData":[TD([makeQuery(id+"F1.opExtrude","SWEPT_FACE",FACE,{"disambiguationData":[OSD([subQ0])]})])],"derivedFrom":makeQuery(id+"F5.opExtrude","SWEPT_EDGE",EDGE,{"disambiguationData":[OSD([subQ1,subQ2])]})});}
            var Q47;
            {var subQ0=sQuery(id+"F0.wireOp",EDGE,"E3");var subQ1=sQuery(id+"F4.wireOp",EDGE,"E71");var subQ2=sQuery(id+"F4.wireOp",EDGE,"E73.trimOffspring");Q47=makeQuery(id+"F5.boolean.opBoolean","COPY",EDGE,{"disambiguationData":[TD([makeQuery(id+"F1.opExtrude","SWEPT_FACE",FACE,{"disambiguationData":[OSD([subQ0])]})])],"derivedFrom":makeQuery(id+"F5.opExtrude","SWEPT_EDGE",EDGE,{"disambiguationData":[OSD([subQ1,subQ2])]})});}
            fillet(context, id + "F11", {"entities" : qUnion([Q0, Q1, Q2, Q3, Q4, Q5, Q6, Q7, Q8, Q9, Q10, Q11, Q12, Q13, Q14, Q15, Q16, Q17, Q18, Q19, Q20, Q21, Q22, Q23, Q24, Q25, Q26, Q27, Q28, Q29, Q30, Q31, Q32, Q33, Q34, Q35, Q36, Q37, Q38, Q39, Q40, Q41, Q42, Q43, Q44, Q45, Q46, Q47]), "radius" : 1.52 * mm, "tangentPropagation" : true, "allowEdgeOverflow" : false});
        }
        {
            var Q0;
            Q0=makeQuery(id+"F8.opFillet","BLEND_EDGE",EDGE,{"blendedFrom":[makeQuery(id+"F7.boolean.opBoolean","COPY",EDGE,{"derivedFrom":makeQuery(id+"F7.opExtrude","SWEPT_EDGE",EDGE,{"disambiguationData":[OSD([sQuery(id+"F6.wireOp",EDGE,"E78"),sQuery(id+"F6.wireOp",EDGE,"E79")])]})}),makeQuery(id+"F3.opShell","OFFSET_FACE",FACE,{"disambiguationData":[OSD([sQuery(id+"F0.wireOp",EDGE,"E2"),sQuery(id+"F0.wireOp",EDGE,"E3"),sQuery(id+"F0.wireOp",EDGE,"E4"),sQuery(id+"F0.wireOp",EDGE,"E5")])]})],"blendedInto":[makeQuery(id+"F3.opShell","OFFSET_FACE",FACE,{"disambiguationData":[OSD([sQuery(id+"F0.wireOp",EDGE,"E2"),sQuery(id+"F0.wireOp",EDGE,"E3"),sQuery(id+"F0.wireOp",EDGE,"E4"),sQuery(id+"F0.wireOp",EDGE,"E5")])]})]});
            var Q1;
            Q1=makeQuery(id+"F8.opFillet","BLEND_EDGE",EDGE,{"blendedFrom":[makeQuery(id+"F7.boolean.opBoolean","COPY",EDGE,{"derivedFrom":makeQuery(id+"F7.opExtrude","SWEPT_EDGE",EDGE,{"disambiguationData":[OSD([sQuery(id+"F6.wireOp",EDGE,"E84"),sQuery(id+"F6.wireOp",EDGE,"E89.trimOffspring")])]})}),makeQuery(id+"F3.opShell","OFFSET_FACE",FACE,{"disambiguationData":[OSD([sQuery(id+"F0.wireOp",EDGE,"E2"),sQuery(id+"F0.wireOp",EDGE,"E3"),sQuery(id+"F0.wireOp",EDGE,"E4"),sQuery(id+"F0.wireOp",EDGE,"E5")])]})],"blendedInto":[makeQuery(id+"F3.opShell","OFFSET_FACE",FACE,{"disambiguationData":[OSD([sQuery(id+"F0.wireOp",EDGE,"E2"),sQuery(id+"F0.wireOp",EDGE,"E3"),sQuery(id+"F0.wireOp",EDGE,"E4"),sQuery(id+"F0.wireOp",EDGE,"E5")])]})]});
            var Q2;
            Q2=makeQuery(id+"F8.opFillet","BLEND_EDGE",EDGE,{"blendedFrom":[makeQuery(id+"F7.boolean.opBoolean","COPY",EDGE,{"derivedFrom":makeQuery(id+"F7.opExtrude","SWEPT_EDGE",EDGE,{"disambiguationData":[OSD([sQuery(id+"F6.wireOp",EDGE,"E82"),sQuery(id+"F6.wireOp",EDGE,"E86.trimOffspring")])]})}),makeQuery(id+"F3.opShell","OFFSET_FACE",FACE,{"disambiguationData":[OSD([sQuery(id+"F0.wireOp",EDGE,"E2"),sQuery(id+"F0.wireOp",EDGE,"E3"),sQuery(id+"F0.wireOp",EDGE,"E4"),sQuery(id+"F0.wireOp",EDGE,"E5")])]})],"blendedInto":[makeQuery(id+"F3.opShell","OFFSET_FACE",FACE,{"disambiguationData":[OSD([sQuery(id+"F0.wireOp",EDGE,"E2"),sQuery(id+"F0.wireOp",EDGE,"E3"),sQuery(id+"F0.wireOp",EDGE,"E4"),sQuery(id+"F0.wireOp",EDGE,"E5")])]})]});
            var Q3;
            Q3=makeQuery(id+"F8.opFillet","BLEND_EDGE",EDGE,{"blendedFrom":[makeQuery(id+"F7.boolean.opBoolean","COPY",EDGE,{"derivedFrom":makeQuery(id+"F7.opExtrude","SWEPT_EDGE",EDGE,{"disambiguationData":[OSD([sQuery(id+"F6.wireOp",EDGE,"E77"),sQuery(id+"F6.wireOp",EDGE,"E82")])]})}),makeQuery(id+"F1.opExtrude","CAP_FACE",FACE,{"disambiguationData":[OSD([sQuery(id+"F0.wireOp",EDGE,"E2"),sQuery(id+"F0.wireOp",EDGE,"E3"),sQuery(id+"F0.wireOp",EDGE,"E4"),sQuery(id+"F0.wireOp",EDGE,"E5")])],"isStart":true})],"blendedInto":[makeQuery(id+"F1.opExtrude","CAP_FACE",FACE,{"disambiguationData":[OSD([sQuery(id+"F0.wireOp",EDGE,"E2"),sQuery(id+"F0.wireOp",EDGE,"E3"),sQuery(id+"F0.wireOp",EDGE,"E4"),sQuery(id+"F0.wireOp",EDGE,"E5")])],"isStart":true})]});
            var Q4;
            Q4=makeQuery(id+"F8.opFillet","BLEND_EDGE",EDGE,{"blendedFrom":[makeQuery(id+"F7.boolean.opBoolean","COPY",EDGE,{"derivedFrom":makeQuery(id+"F7.opExtrude","SWEPT_EDGE",EDGE,{"disambiguationData":[OSD([sQuery(id+"F6.wireOp",EDGE,"E83"),sQuery(id+"F6.wireOp",EDGE,"E87.trimOffspring")])]})}),makeQuery(id+"F1.opExtrude","CAP_FACE",FACE,{"disambiguationData":[OSD([sQuery(id+"F0.wireOp",EDGE,"E2"),sQuery(id+"F0.wireOp",EDGE,"E3"),sQuery(id+"F0.wireOp",EDGE,"E4"),sQuery(id+"F0.wireOp",EDGE,"E5")])],"isStart":true})],"blendedInto":[makeQuery(id+"F1.opExtrude","CAP_FACE",FACE,{"disambiguationData":[OSD([sQuery(id+"F0.wireOp",EDGE,"E2"),sQuery(id+"F0.wireOp",EDGE,"E3"),sQuery(id+"F0.wireOp",EDGE,"E4"),sQuery(id+"F0.wireOp",EDGE,"E5")])],"isStart":true})]});
            var Q5;
            Q5=makeQuery(id+"F8.opFillet","BLEND_EDGE",EDGE,{"blendedFrom":[makeQuery(id+"F7.boolean.opBoolean","COPY",EDGE,{"derivedFrom":makeQuery(id+"F7.opExtrude","SWEPT_EDGE",EDGE,{"disambiguationData":[OSD([sQuery(id+"F6.wireOp",EDGE,"E85"),sQuery(id+"F6.wireOp",EDGE,"E88.trimOffspring")])]})}),makeQuery(id+"F1.opExtrude","CAP_FACE",FACE,{"disambiguationData":[OSD([sQuery(id+"F0.wireOp",EDGE,"E2"),sQuery(id+"F0.wireOp",EDGE,"E3"),sQuery(id+"F0.wireOp",EDGE,"E4"),sQuery(id+"F0.wireOp",EDGE,"E5")])],"isStart":true})],"blendedInto":[makeQuery(id+"F1.opExtrude","CAP_FACE",FACE,{"disambiguationData":[OSD([sQuery(id+"F0.wireOp",EDGE,"E2"),sQuery(id+"F0.wireOp",EDGE,"E3"),sQuery(id+"F0.wireOp",EDGE,"E4"),sQuery(id+"F0.wireOp",EDGE,"E5")])],"isStart":true})]});
            var Q6;
            Q6=makeQuery(id+"F1.opExtrude","CAP_EDGE",EDGE,{"disambiguationData":[OSD([sQuery(id+"F0.wireOp",EDGE,"E2")])],"isStart":true});
            chamfer(context, id + "F12", {"entities" : qUnion([Q0, Q1, Q2, Q3, Q4, Q5, Q6]), "width" : 1.27 * mm, "tangentPropagation" : true});
        }
        {
            var Q0;
            Q0=makeQuery(id+"F5.boolean.opBoolean","INTERSECT",EDGE,{"derivedFrom":[makeQuery(id+"F1.opExtrude","SWEPT_FACE",FACE,{"disambiguationData":[OSD([sQuery(id+"F0.wireOp",EDGE,"E3")])]}),makeQuery(id+"F5.opExtrude","SWEPT_FACE",FACE,{"disambiguationData":[OSD([sQuery(id+"F4.wireOp",EDGE,"E24")])]})]});
            var Q1;
            Q1=makeQuery(id+"F9.opFillet","BLEND_EDGE",EDGE,{"blendedFrom":[makeQuery(id+"F3.opShell","OFFSET_EDGE",EDGE,{"disambiguationData":[OSD([sQuery(id+"F0.wireOp",EDGE,"E2"),sQuery(id+"F0.wireOp",EDGE,"E3")])]}),makeQuery(id+"F5.boolean.opBoolean","COPY",FACE,{"derivedFrom":makeQuery(id+"F5.opExtrude","SWEPT_FACE",FACE,{"disambiguationData":[OSD([sQuery(id+"F4.wireOp",EDGE,"E24")])]})})],"blendedInto":[makeQuery(id+"F5.boolean.opBoolean","COPY",FACE,{"derivedFrom":makeQuery(id+"F5.opExtrude","SWEPT_FACE",FACE,{"disambiguationData":[OSD([sQuery(id+"F4.wireOp",EDGE,"E24")])]})})]});
            var Q2;
            Q2=makeQuery(id+"F5.boolean.opBoolean","INTERSECT",EDGE,{"derivedFrom":[makeQuery(id+"F1.opExtrude","SWEPT_FACE",FACE,{"disambiguationData":[OSD([sQuery(id+"F0.wireOp",EDGE,"E3")])]}),makeQuery(id+"F5.opExtrude","SWEPT_FACE",FACE,{"disambiguationData":[OSD([sQuery(id+"F4.wireOp",EDGE,"E28")])]})]});
            var Q3;
            Q3=makeQuery(id+"F9.opFillet","BLEND_EDGE",EDGE,{"blendedFrom":[makeQuery(id+"F3.opShell","OFFSET_EDGE",EDGE,{"disambiguationData":[OSD([sQuery(id+"F0.wireOp",EDGE,"E3"),sQuery(id+"F0.wireOp",EDGE,"E4")])]}),makeQuery(id+"F5.boolean.opBoolean","COPY",FACE,{"derivedFrom":makeQuery(id+"F5.opExtrude","SWEPT_FACE",FACE,{"disambiguationData":[OSD([sQuery(id+"F4.wireOp",EDGE,"E28")])]})})],"blendedInto":[makeQuery(id+"F5.boolean.opBoolean","COPY",FACE,{"derivedFrom":makeQuery(id+"F5.opExtrude","SWEPT_FACE",FACE,{"disambiguationData":[OSD([sQuery(id+"F4.wireOp",EDGE,"E28")])]})})]});
            chamfer(context, id + "F13", {"entities" : qUnion([Q0, Q1, Q2, Q3]), "width" : 0.64 * mm, "tangentPropagation" : true});
        }
    });
